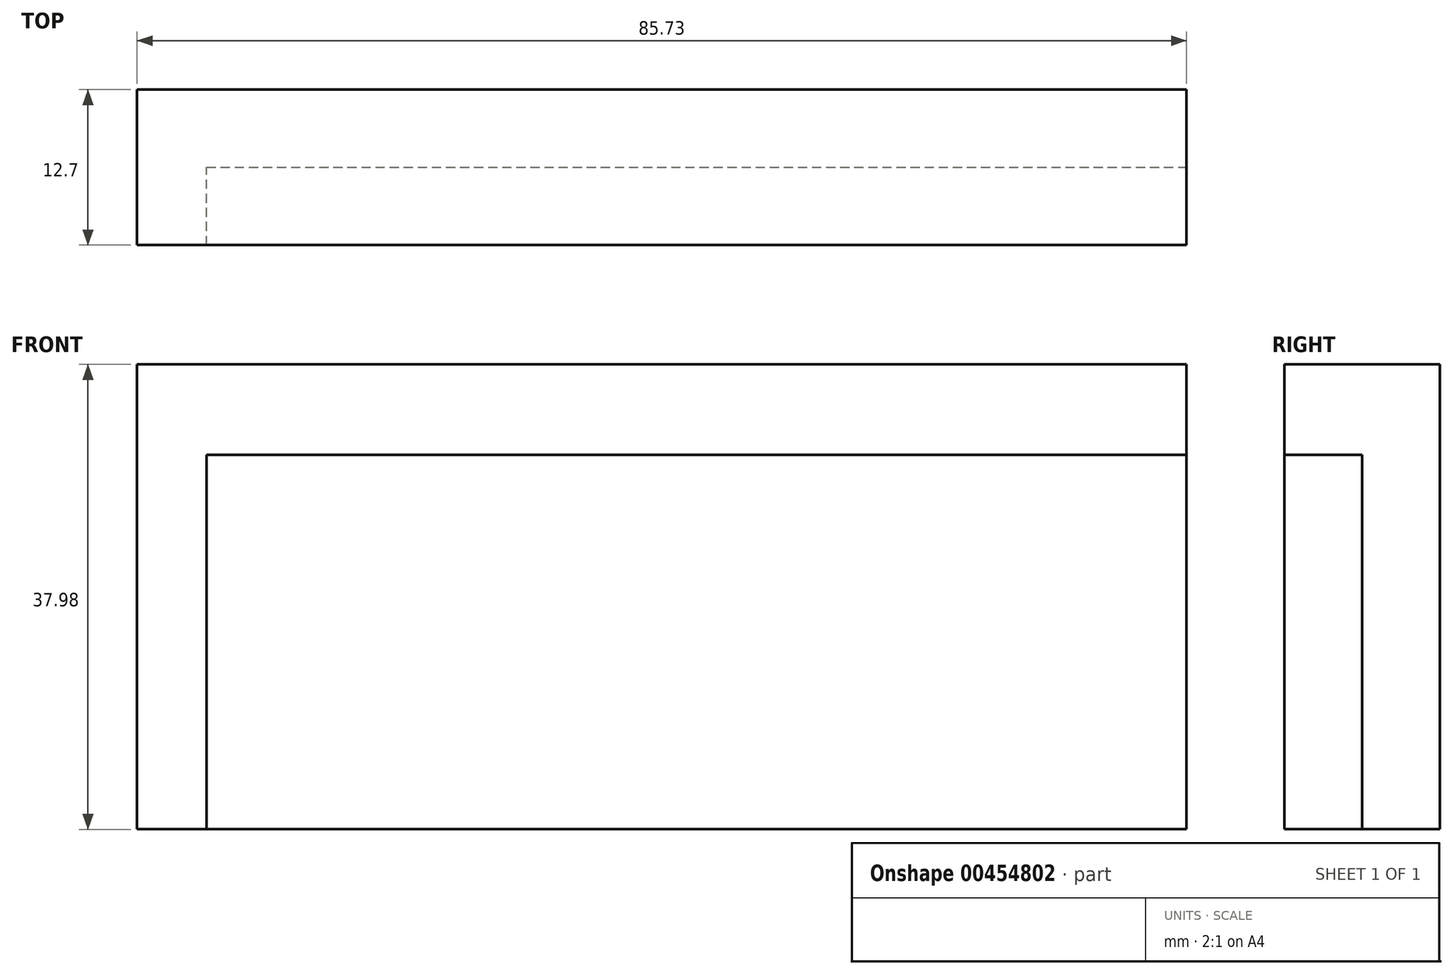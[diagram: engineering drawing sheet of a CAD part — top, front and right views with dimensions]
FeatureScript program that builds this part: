
annotation { "Feature Type Name" : "Feature", "Feature Type Description" : "" }
export const myFeature = defineFeature(function(context is Context, id is Id, definition is map)
    precondition{}
    {
        {
            var Q0;
            Q0=qCreatedBy(makeId("Front.planeOp"),FACE);
            var sketch = newSketch(context, id + "F0", { "sketchPlane" : qUnion([Q0])});
            skLineSegment(sketch, "E0", {"start": v(0, 1.47) * mm, "end": v(85.73, 1.47) * mm});
            skLineSegment(sketch, "E1", {"start": v(85.73, 1.47) * mm, "end": v(85.73, 39.45) * mm});
            skLineSegment(sketch, "E2", {"start": v(85.73, 39.45) * mm, "end": v(0, 39.45) * mm});
            skLineSegment(sketch, "E3", {"start": v(0, 39.45) * mm, "end": v(0, 1.47) * mm});
            skSolve(sketch);
        }
        {
            var Q0;
            Q0=makeQuery(id+"F0.imprint","IMPRINT",FACE,{"disambiguationData":[TD([[makeQuery(id+"F0.imprint","IMPRINT",EDGE,{"derivedFrom":sQuery(id+"F0.wireOp",EDGE,"E0")}),1.0]])]});
            extrude(context, id + "F1", {"entities" : qUnion([Q0]), "depth" : 6.35 * mm});
        }
        {
            var Q0;
            Q0=makeQuery(id+"F1.opExtrude","CAP_FACE",FACE,{"disambiguationData":[OSD([sQuery(id+"F0.wireOp",EDGE,"E0"),sQuery(id+"F0.wireOp",EDGE,"E1"),sQuery(id+"F0.wireOp",EDGE,"E2"),sQuery(id+"F0.wireOp",EDGE,"E3")])],"isStart":false});
            var sketch = newSketch(context, id + "F2", { "sketchPlane" : qUnion([Q0])});
            skLineSegment(sketch, "E4", {"start": v(0, 1.47) * mm, "end": v(5.68, 1.47) * mm});
            skLineSegment(sketch, "E5", {"start": v(5.68, 1.47) * mm, "end": v(5.68, 32.08) * mm});
            skLineSegment(sketch, "E6", {"start": v(5.68, 32.08) * mm, "end": v(85.73, 32.08) * mm});
            skLineSegment(sketch, "E7", {"start": v(85.73, 32.08) * mm, "end": v(85.73, 39.45) * mm});
            skLineSegment(sketch, "E8", {"start": v(85.73, 39.45) * mm, "end": v(0, 39.45) * mm});
            skLineSegment(sketch, "E9", {"start": v(0, 39.45) * mm, "end": v(0, 1.47) * mm});
            skSolve(sketch);
        }
        {
            var Q0;
            Q0=makeQuery(id+"F2.imprint","IMPRINT",FACE,{"disambiguationData":[TD([[makeQuery(id+"F2.imprint","IMPRINT",EDGE,{"derivedFrom":sQuery(id+"F2.wireOp",EDGE,"E4")}),1.0]])]});
            extrude(context, id + "F3", {"entities" : qUnion([Q0]), "operationType" : NewBodyOperationType.ADD, "depth" : 6.35 * mm});
        }
    });
